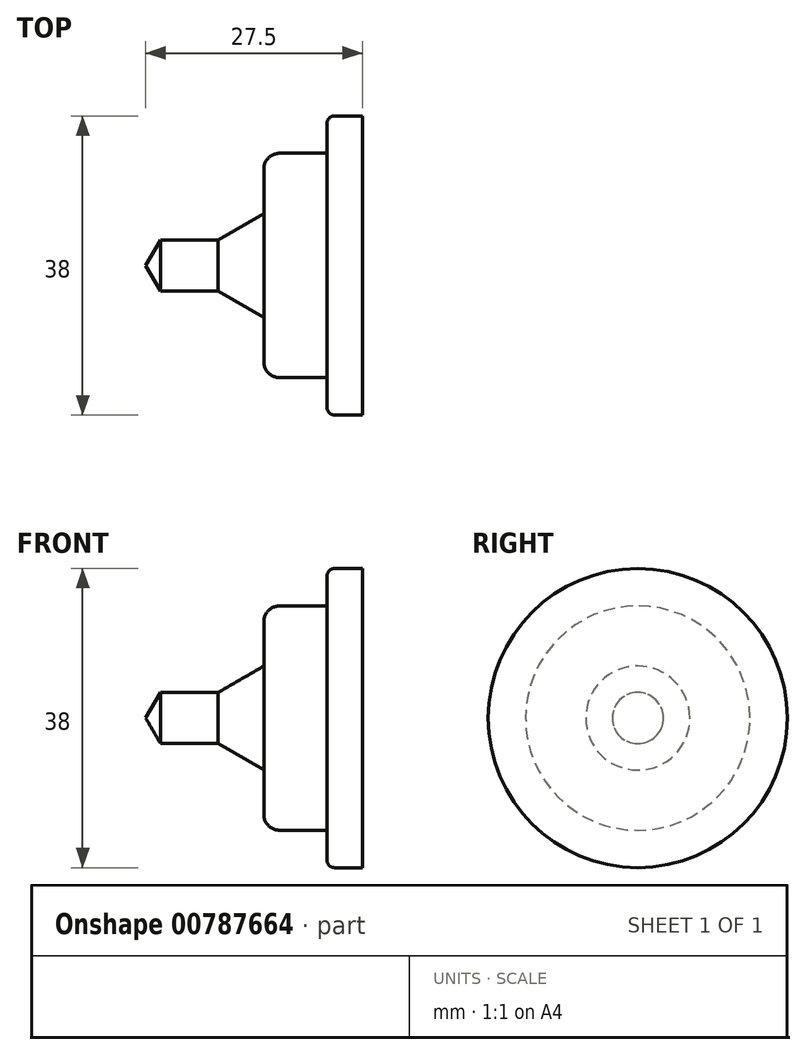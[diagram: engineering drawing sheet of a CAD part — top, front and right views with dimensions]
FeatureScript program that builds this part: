
annotation { "Feature Type Name" : "Feature", "Feature Type Description" : "" }
export const myFeature = defineFeature(function(context is Context, id is Id, definition is map)
    precondition{}
    {
        {
            var Q0;
            Q0=qCreatedBy(makeId("Front.planeOp"),FACE);
            var sketch = newSketch(context, id + "F0", { "sketchPlane" : qUnion([Q0])});
            skLineSegment(sketch, "E0", {"start": v(27.5, 19) * mm, "end": v(24, 19) * mm});
            skLineSegment(sketch, "E1", {"start": v(23, 18) * mm, "end": v(23, 14.25) * mm});
            skLineSegment(sketch, "E2", {"start": v(23, 14.25) * mm, "end": v(17, 14.25) * mm});
            skLineSegment(sketch, "E3", {"start": v(15, 12.25) * mm, "end": v(15, 6.61) * mm});
            skLineSegment(sketch, "E4", {"start": v(15, 6.61) * mm, "end": v(9.18, 3.25) * mm});
            skLineSegment(sketch, "E5", {"start": v(9.18, 3.25) * mm, "end": v(1.88, 3.25) * mm});
            skLineSegment(sketch, "E6", {"start": v(1.88, 3.25) * mm, "end": v(0, 0) * mm});
            skLineSegment(sketch, "E7", {"start": v(0, 0) * mm, "end": v(27.5, 0) * mm});
            skLineSegment(sketch, "E8", {"start": v(27.5, 0) * mm, "end": v(27.5, 19) * mm});
            skPoint(sketch, "E9.visualSharp", {"position": v(23, 19) * mm});
            skArc(sketch, "E9.filletArc", {"start": v(24, 19) * mm, "mid": v(23.3, 18.7) * mm, "end": v(23, 18) * mm});
            skPoint(sketch, "E10.visualSharp", {"position": v(15, 14.25) * mm});
            skArc(sketch, "E10.filletArc", {"start": v(17, 14.25) * mm, "mid": v(15.59, 13.66) * mm, "end": v(15, 12.25) * mm});
            skSolve(sketch);
        }
        {
            var Q0;
            Q0=makeQuery(id+"F0.imprint","IMPRINT",FACE,{"disambiguationData":[TD([[makeQuery(id+"F0.imprint","IMPRINT",EDGE,{"derivedFrom":sQuery(id+"F0.wireOp",EDGE,"E0")}),1.0]])]});
            var Q1;
            Q1=sQuery(id+"F0.wireOp",EDGE,"E7");
            revolve(context, id + "F1", {"surfaceOperationType" : NewSurfaceOperationType.NEW, "entities" : qUnion([Q0]), "axis" : qUnion([Q1]), "revolveType" : RevolveType.FULL});
        }
    });
